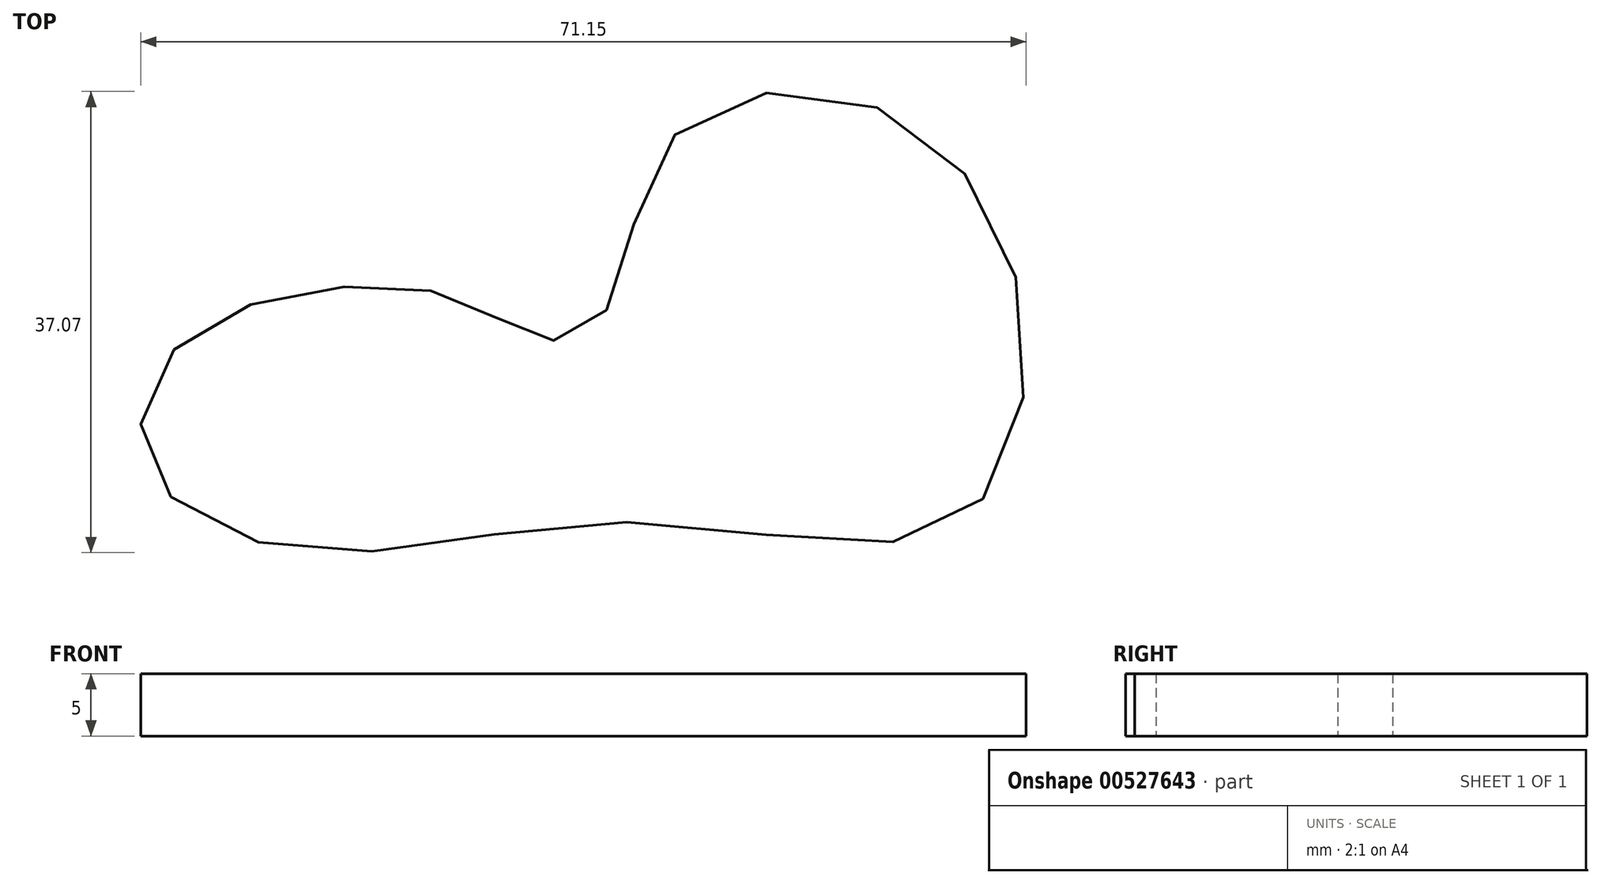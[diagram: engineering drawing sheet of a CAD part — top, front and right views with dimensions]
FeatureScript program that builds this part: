
annotation { "Feature Type Name" : "Feature", "Feature Type Description" : "" }
export const myFeature = defineFeature(function(context is Context, id is Id, definition is map)
    precondition{}
    {
        {
            var Q0;
            Q0=qCreatedBy(makeId("Top.planeOp"),FACE);
            var sketch = newSketch(context, id + "F0", { "sketchPlane" : qUnion([Q0])});
            skFitSpline(sketch, "E0", {"points": [v(-50.72, 23.08) * mm, v(-38.24, 28.03) * mm, v(-26.94, 26.84) * mm, v(-21, 23.87) * mm, v(-15.85, 26.45) * mm, v(-10.7, 40.12) * mm, v(5.94, 42.5) * mm, v(17.43, 26.65) * mm, v(11.89, 9.01) * mm, v(-13.67, 9.21) * mm, v(-39.42, 6.83) * mm, v(-52.7, 13.57) * mm, v(-50.72, 23.08) * mm]});
            skSolve(sketch);
        }
        {
            var Q0;
            Q0=makeQuery(id+"F0.imprint","IMPRINT",FACE,{"disambiguationData":[TD([[makeQuery(id+"F0.imprint","IMPRINT",EDGE,{"derivedFrom":sQuery(id+"F0.wireOp",EDGE,"E0")}),-1.0]])]});
            extrude(context, id + "F1", {"entities" : qUnion([Q0]), "depth" : 5 * mm, "offsetDistance" : 25 * mm});
        }
    });
